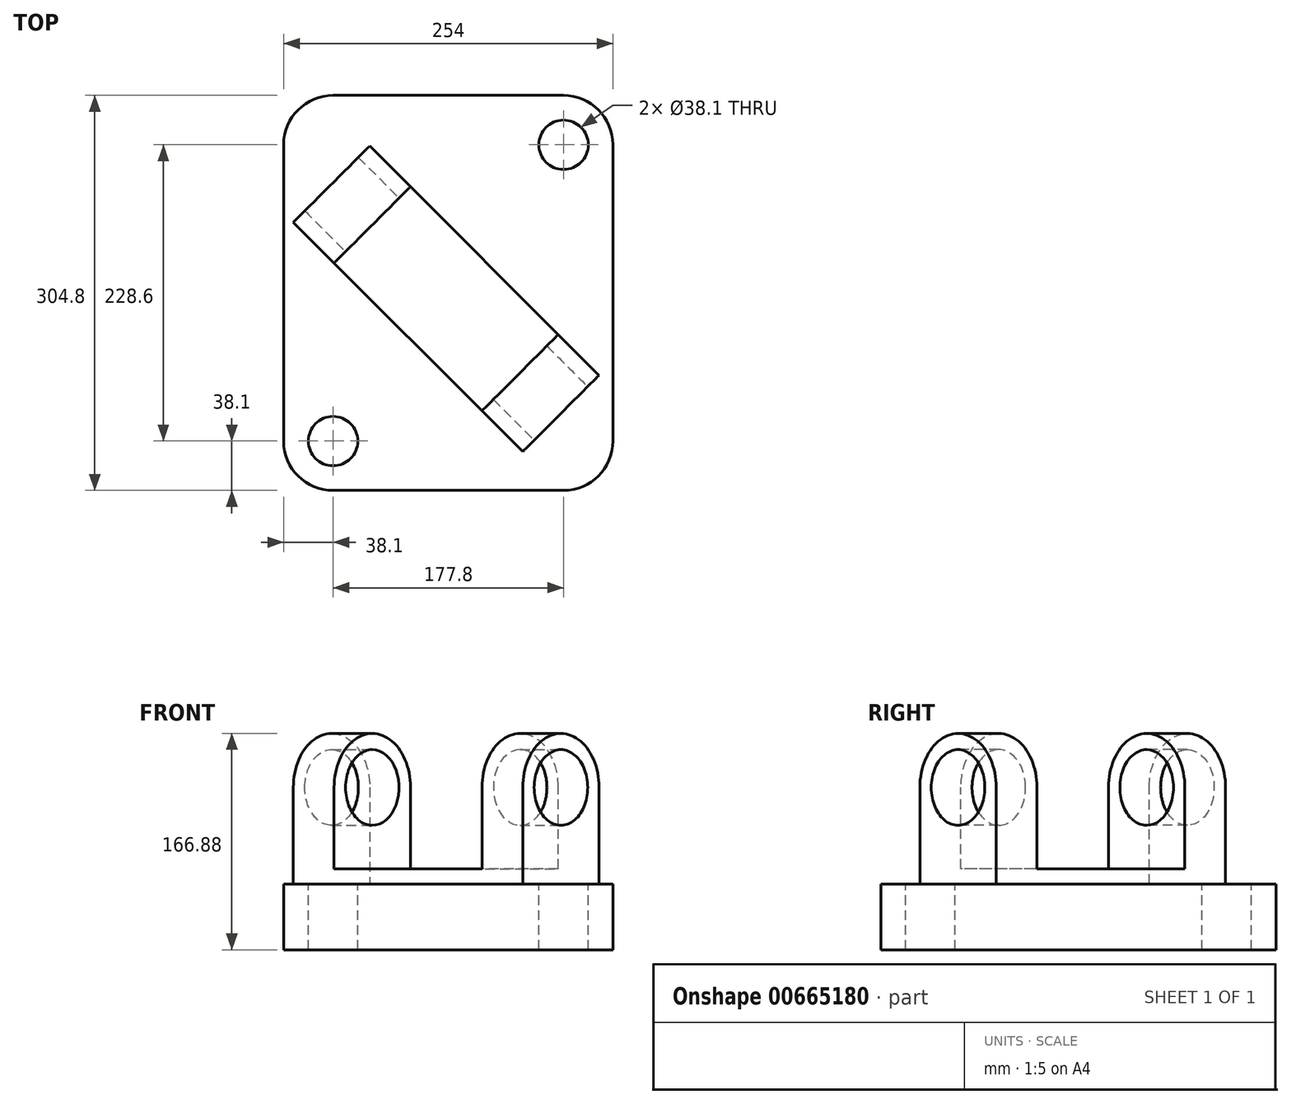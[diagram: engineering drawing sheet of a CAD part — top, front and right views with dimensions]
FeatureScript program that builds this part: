
annotation { "Feature Type Name" : "Feature", "Feature Type Description" : "" }
export const myFeature = defineFeature(function(context is Context, id is Id, definition is map)
    precondition{}
    {
        {
            var Q0;
            Q0=qCreatedBy(makeId("Top.planeOp"),FACE);
            var sketch = newSketch(context, id + "F0", { "sketchPlane" : qUnion([Q0])});
            skLineSegment(sketch, "E0", {"start": v(38.1, 0) * mm, "end": v(215.9, 0) * mm});
            skLineSegment(sketch, "E1", {"start": v(254, 38.1) * mm, "end": v(254, 266.7) * mm});
            skLineSegment(sketch, "E2", {"start": v(215.9, 304.8) * mm, "end": v(38.1, 304.8) * mm});
            skLineSegment(sketch, "E3", {"start": v(0, 266.7) * mm, "end": v(0, 38.1) * mm});
            skPoint(sketch, "E4.visualSharp", {"position": v(0, 304.8) * mm});
            skArc(sketch, "E4.filletArc", {"start": v(38.1, 304.8) * mm, "mid": v(11.16, 293.64) * mm, "end": v(0, 266.7) * mm});
            skPoint(sketch, "E5.visualSharp", {"position": v(254, 304.8) * mm});
            skArc(sketch, "E5.filletArc", {"start": v(254, 266.7) * mm, "mid": v(242.84, 293.64) * mm, "end": v(215.9, 304.8) * mm});
            skPoint(sketch, "E6.visualSharp", {"position": v(254, 0) * mm});
            skArc(sketch, "E6.filletArc", {"start": v(215.9, 0) * mm, "mid": v(242.84, 11.16) * mm, "end": v(254, 38.1) * mm});
            skPoint(sketch, "E7.visualSharp", {"position": v(0, 0) * mm});
            skArc(sketch, "E7.filletArc", {"start": v(0, 38.1) * mm, "mid": v(11.16, 11.16) * mm, "end": v(38.1, 0) * mm});
            skSolve(sketch);
        }
        {
            var Q0;
            Q0=makeQuery(id+"F0.imprint","IMPRINT",FACE,{"disambiguationData":[TD([[makeQuery(id+"F0.imprint","IMPRINT",EDGE,{"derivedFrom":sQuery(id+"F0.wireOp",EDGE,"E0")}),1.0]])]});
            extrude(context, id + "F1", {"entities" : qUnion([Q0]), "depth" : 50.8 * mm, "offsetDistance" : 25.4 * mm});
        }
        {
            var Q0;
            Q0=makeQuery(id+"F1.opExtrude","CAP_FACE",FACE,{"disambiguationData":[OSD([sQuery(id+"F0.wireOp",EDGE,"E0"),sQuery(id+"F0.wireOp",EDGE,"E1"),sQuery(id+"F0.wireOp",EDGE,"E2"),sQuery(id+"F0.wireOp",EDGE,"E3"),sQuery(id+"F0.wireOp",EDGE,"E4.filletArc"),sQuery(id+"F0.wireOp",EDGE,"E5.filletArc"),sQuery(id+"F0.wireOp",EDGE,"E6.filletArc"),sQuery(id+"F0.wireOp",EDGE,"E7.filletArc")])],"isStart":false});
            var sketch = newSketch(context, id + "F2", { "sketchPlane" : qUnion([Q0])});
            skLineSegment(sketch, "E8", {"start": v(7.5, 206.88) * mm, "end": v(66.4, 265.8) * mm});
            skLineSegment(sketch, "E9", {"start": v(66.4, 265.8) * mm, "end": v(243.31, 88.88) * mm});
            skLineSegment(sketch, "E10", {"start": v(243.31, 88.88) * mm, "end": v(184.4, 29.97) * mm});
            skLineSegment(sketch, "E11", {"start": v(184.4, 29.97) * mm, "end": v(7.5, 206.88) * mm});
            skPoint(sketch, "E12.0", {"position": v(215.9, 266.7) * mm});
            skPoint(sketch, "E13.0", {"position": v(38.1, 38.1) * mm});
            skSolve(sketch);
        }
        {
            var Q0;
            Q0=sQuery(id+"F2.wireOp",VERTEX,"E11.start");
            var Q1;
            Q1=sQuery(id+"F2.wireOp",EDGE,"E11");
            cPlane(context, id + "F3", {"entities" : qUnion([Q0, Q1]), "cplaneType" : CPlaneType.LINE_POINT, "offset" : 25.4 * mm, "width" : 152.4 * mm, "height" : 152.4 * mm});
        }
        {
            var Q0;
            Q0=qCreatedBy(id+"F3.planeOp",FACE);
            var sketch = newSketch(context, id + "F4", { "sketchPlane" : qUnion([Q0])});
            skLineSegment(sketch, "E14.0", {"start": v(-234.9, 50.8) * mm, "end": v(-151.59, 50.8) * mm});
            skLineSegment(sketch, "E15", {"start": v(-151.59, 50.8) * mm, "end": v(-151.59, 125.22) * mm});
            skLineSegment(sketch, "E16", {"start": v(-234.9, 125.22) * mm, "end": v(-234.9, 50.8) * mm});
            skArc(sketch, "E17", {"start": v(-151.59, 125.22) * mm, "mid": v(-193.24, 166.88) * mm, "end": v(-234.9, 125.22) * mm});
            skCircle(sketch, "E18", {"center": v(-193.24, 125.22) * mm, "radius": 29.21 * mm});
            skSolve(sketch);
        }
        {
            var Q0;
            Q0=makeQuery(id+"F4.imprint","IMPRINT",FACE,{"disambiguationData":[TD([[makeQuery(id+"F4.imprint","IMPRINT",EDGE,{"derivedFrom":sQuery(id+"F4.wireOp",EDGE,"E14.0")}),1.0]])]});
            var Q1;
            Q1=sQuery(id+"F2.wireOp",VERTEX,"E8.start");
            extrude(context, id + "F5", {"entities" : qUnion([Q0]), "operationType" : NewBodyOperationType.ADD, "endBound" : BoundingType.UP_TO_VERTEX, "depth" : 25.4 * mm, "endBoundEntityVertex" : qUnion([Q1]), "offsetDistance" : 25.4 * mm});
        }
        {
            var Q0;
            Q0=makeQuery(id+"F5.opExtrude","SWEPT_FACE",FACE,{"disambiguationData":[OSD([sQuery(id+"F4.wireOp",EDGE,"E15")])]});
            var sketch = newSketch(context, id + "F6", { "sketchPlane" : qUnion([Q0])});
            skLineSegment(sketch, "E19", {"start": v(-141, 166.88) * mm, "end": v(109.2, 166.88) * mm});
            skLineSegment(sketch, "E20", {"start": v(-96.54, 166.88) * mm, "end": v(-96.54, 62.48) * mm});
            skLineSegment(sketch, "E21", {"start": v(-96.54, 62.48) * mm, "end": v(64.75, 62.48) * mm});
            skLineSegment(sketch, "E22", {"start": v(64.75, 62.48) * mm, "end": v(64.75, 166.88) * mm});
            skSolve(sketch);
        }
        {
            var Q0;
            {var subQ0=sQuery(id+"F6.wireOp",EDGE,"E20");var subQ1=sQuery(id+"F6.wireOp",EDGE,"E19");var subQ2=makeQuery(id+"F6.imprint","INTERSECT",VERTEX,{"derivedFrom":[subQ1,subQ0]});Q0=makeQuery(id+"F6.imprint","IMPRINT",FACE,{"disambiguationData":[TD([[makeQuery(id+"F6.imprint","IMPRINT",EDGE,{"disambiguationData":[TD([[subQ2,-1.0]])],"derivedFrom":subQ1}),-1.0]])]});}
            var Q1;
            {var subQ0=sQuery(id+"F6.wireOp",EDGE,"E21");Q1=makeQuery(id+"F6.imprint","IMPRINT",FACE,{"disambiguationData":[TD([[makeQuery(id+"F6.imprint","IMPRINT",EDGE,{"derivedFrom":subQ0}),1.0]])]});}
            extrude(context, id + "F7", {"entities" : qUnion([Q0, Q1]), "operationType" : NewBodyOperationType.REMOVE, "endBound" : BoundingType.THROUGH_ALL, "oppositeDirection" : true, "depth" : 25.4 * mm, "offsetDistance" : 25.4 * mm});
        }
        {
            var Q0;
            Q0=sQuery(id+"F2.wireOp",VERTEX,"E13.0");
            var Q1;
            Q1=sQuery(id+"F2.wireOp",VERTEX,"E12.0");
            var Q2;
            Q2=makeQuery(id+"F1.opExtrude","SWEPT_BODY",BODY,{"disambiguationData":[OSD([sQuery(id+"F0.wireOp",EDGE,"E0"),sQuery(id+"F0.wireOp",EDGE,"E1"),sQuery(id+"F0.wireOp",EDGE,"E2"),sQuery(id+"F0.wireOp",EDGE,"E3"),sQuery(id+"F0.wireOp",EDGE,"E4.filletArc"),sQuery(id+"F0.wireOp",EDGE,"E5.filletArc"),sQuery(id+"F0.wireOp",EDGE,"E6.filletArc"),sQuery(id+"F0.wireOp",EDGE,"E7.filletArc")])]});
            hole(context, id + "F8", {"style" : HoleStyle.SIMPLE, "endStyle" : HoleEndStyle.THROUGH, "holeDiameter" : 38.1 * mm, "majorDiameter" : 6.35 * mm, "isTappedThrough" : true, "tappedDepth" : 12.7 * mm, "tapClearance" : 3, "locations" : qUnion([Q0, Q1]), "scope" : qUnion([Q2])});
        }
    });
